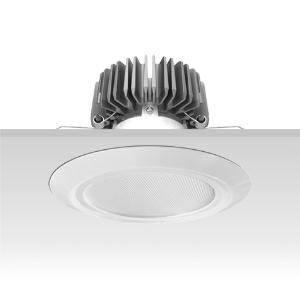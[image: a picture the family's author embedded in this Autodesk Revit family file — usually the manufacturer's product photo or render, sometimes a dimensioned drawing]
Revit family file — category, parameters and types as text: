
# Revit family: 3f_filippi_-_3f_reno_bianco_ampio_3f_filippi_-_30691_a01037_-_3f_reno_200_wh_4000-930_dali_wide___vs_wh_bcf3
name_source: partatom
category: Lighting Fixtures
units: mm (PartAtom-declared; Revit-internal decimal feet)

## family parameters
Cut with Voids When Loaded = No
Host = Face
Light Source = No
Part Type = Normal
Room Calculation Point = No
Round Connector Dimension = Use Diameter
Shared = No

## types (1)
- 3F Filippi - 3F Reno Bianco Ampio (1 x LED, 2801 lm, 43 W, 3000 K)
    Apparent Load = 43 VA
    Approval mark = CE
    CIE Flux Codes = 75 94 99 100 100
    Color Rendering = 90
    Color Temperature = 3000 K
    Control Gear = Electronic transformer
    Default Elevation = 1800 mm
    Description = ILLUMINOTECHNICAL
Luminous efficiency 100% (DLOR 100%, ULOR 0%).
Initial luminous flux of the luminaire 2801 lm.
Direct symmetric wide distribution.
Installation Interdistance Transv.D = 1.16 x hu - Long.D = 1.14 x hu.
Tabular UGR (CIE 117 - 4H-8H; S=0.25H; 70/50/20): RUG 22.1 - 22.
Beam angle: 74° - 74°.
Luminous efficacy 65 lm/W.
Lifetime (L90/B10): 30000 h. (tq+25°C)
Lifetime (L85/B10): 50000 h. (tq+25°C)
Lifetime (L70/B10): 80000 h. (tq+25°C)
Sudden decreased luminous flux after 50000 hours: 0% (C0).
Photobiological safety in compliance with IEC/TR 62778: RG1 low risk, (IEC 62471).
In compliance with IEC/EN 62722-2-1 - IEC/EN 62717 standards.

SOURCE
Compact LED module 4000/930.
Energy efficiency class (UE 2019/2020 - UE 2019/2015): F.
CIE 13.3 Colour rendering index: CRI >90 (R9 >50%).
IES TM-30 Fidelity Index: Rf = 92 Rg = 101.
CCT nominal colour temperature 3000 K.
Colour initial tolerance (MacAdam): SDCM 3.
Zhaga Book 3 compliant.

MECHANICAL
Passive heat dissipator in die-casting aluminium, oversized, for optimum thermal management of the LED module.
Parabolic element with graduated/concentric rings in white polycarbonate.
Transparent external lens with glossy and satin differentiated surfaces, with a cooling and anti-insect system in methacrylate (PMMA).
Fastening spring clips in stainless steel.
Dimensions: diameter 226 mm, height 146 mm. Weight 1.88 kg.
IP44 protection degree for exposed part, IP20 for recessed part.
Mechanical strength to impacts IK06 (1 joule).
Glow-wire test resistance 650°C.

ELECTRICAL
Wiring on a separate unit.
Halogen Free DALI-2 DATI (Parts 251, 252, 253), PUSH-DIM, electronic wiring 230V-50/60Hz, power factor 0.97 at full load, THD <25%, constant output current, SELV, class II, 1 driver, 1 DALI addresse.
Power of the luminaire 43 W.
ENEC - CE.
SAFE FLICKER: PstLM=<1 and SVM=<0.4 (IEC TR 61547-1 and IEC TR 63158), to ensure a more comfortable and safe light.
Luminaire compliant with EN 60598-2-22 for power supply from a centralised emergency system CPSS (Central Power Supply System), not incorporated in the luminaire - high risk areas excluded. The default power and flux are 100% in AC and 100% in DC.
Ambient temperature from 0°C to +25°C.
Temperature class T6 max 85°C.
Relative humidity UR: <85%.

INSTALLATION
Pull-up recessed fitting.
False ceiling carving: 200 mm.
All accessories dedicated to this product are available on the Catalog and on our website www.3F-Filippi.com.

ACCESSORIES
A01037 - Anti-glare microprismatic VS moulded glass, tempered, not flammable, locked and in line with the trim, in white polycarbonate.

APPLICATIONS
Environments: architectural, commercial, exhibition areas, transit areas, corridors, shops, display windows, service areas.
In false ceilings with narrow voids.

LIGHT MANAGEMENT
Recommended minimum setting: 10%.
The luminaire, equipped with (DALI-2 DATI) driver, can be controlled manually with 3F Easy Dim technology or automatically/manually with wired or wireless DALI/D2D control systems.
The D2D driver guarantees interoperability with other devices with the same certification by making the following information available:
Device Data (Part 251), Energy Report (Part 252), Diagnosis & Maintenance (Part 253).
In electrical systems without a regulation system (manual or automatic) and DALI bus, a suitable jumper must be made on the DA-DA terminals of the appliance.

WARNING
Luminaire designed for disposal/recycling at end-of-life.
Replaceable (LED only) light source by a professional. Replaceable control gear by a professional.
    Height = 0 mm  [stored 0 ft]
    Lamp = 1 x LED
    Lamp Light Flux = 2801 lm
    Lamp Power = 43 W
    Lamp count = 1
    Length = 226 mm
    Lifetime = 50000 h
    Luminous efficacy = 65 lm/W
    Manufacturer = 3F Filippi
    ModVariant = No
    Model = 3F Filippi - 30691+A01037 - 3F Reno 200 WH 4000-930 DALI WIDE + VS WH
    Mounting Place = Ceiling
    Mounting Type = Recessed
    Number of Poles = 1
    OnlyDefault = Yes
    Power Factor = 1
    Product Name = 3F Filippi - 3F Reno Bianco Ampio
    Product group = recessed luminaire
    ProductGroupID = 4
    Protection Class = Protection class II
    Protection Degree = IP 20
    RLX_Detail_Level = 1
    RLX_Emergency_Light_Flux = 0 lm
    RLX_Emergency_Type = 0
    RLX_Emergency_Type_DB = No
    RlxData = <blob elided: 96165 chars, md5=55fbb120>
    Socket = socket
    Standby Power = 0 W
    System Light Flux = 2801 lm
    System Power = 43 W
    Type Comments = Product without accessories
    Type Image = 3ffilippi_3f_reno_200_wh_vs_smp.jpg
    URL = http://relux.com
    VarID = ---
    Voltage = 0 V
    Weight = 0.00 kg
    Width = 0 mm  [stored 0 ft]

note: [stored X ft] marks values corroborated as IEEE doubles in the binary element streams (Revit-internal decimal feet)

## geometry (parser evidence)
native form markers: Blend x4, Sweep x11
no freeform markers — native parametric forms only
